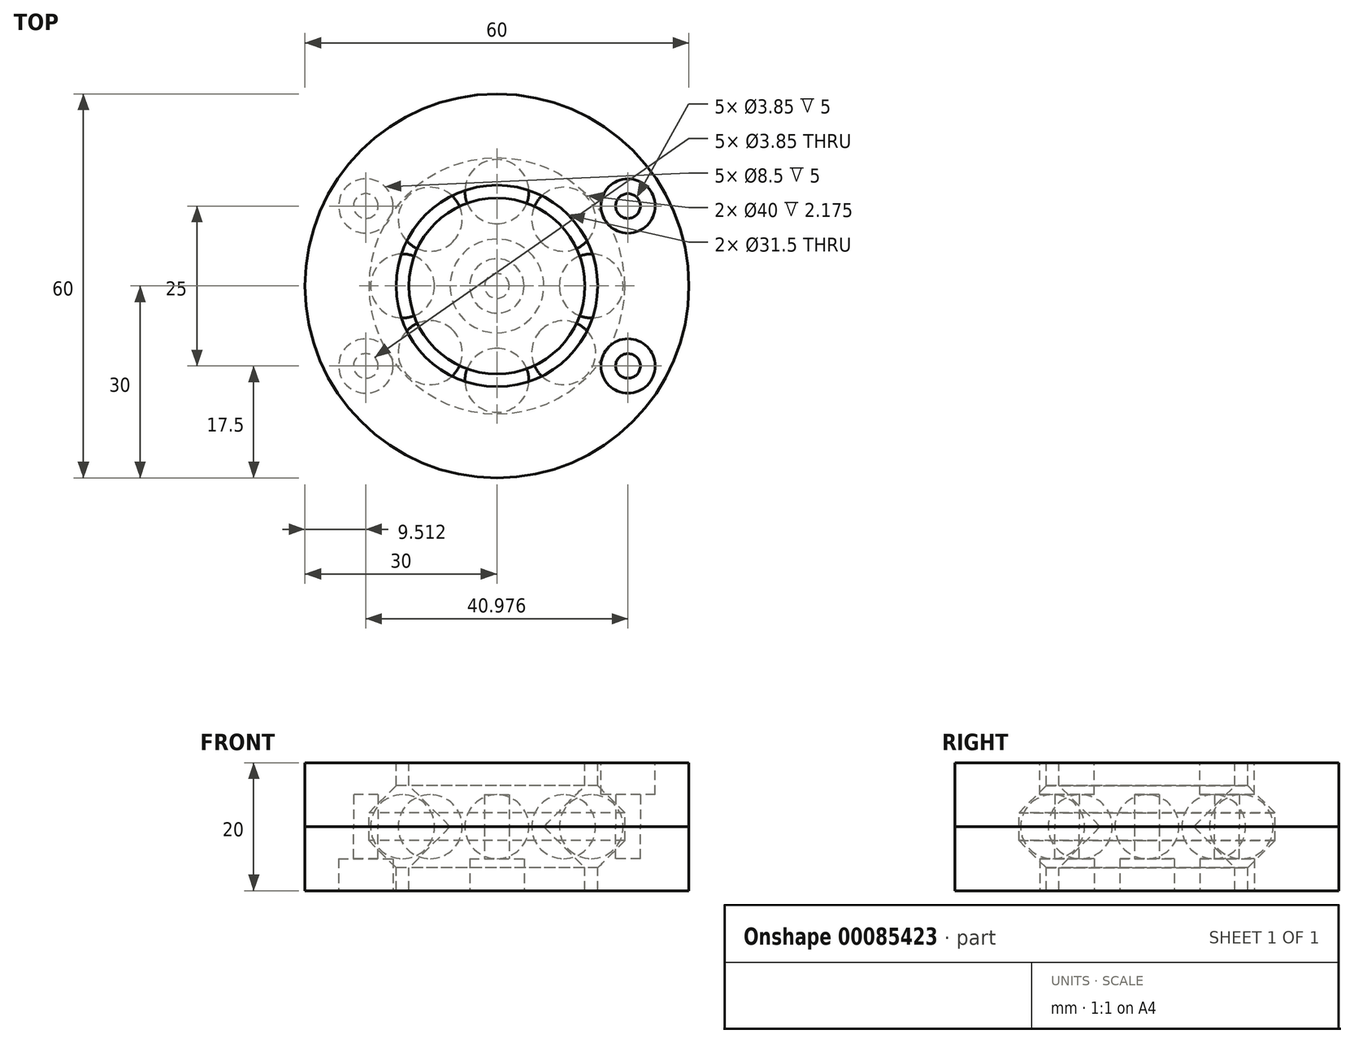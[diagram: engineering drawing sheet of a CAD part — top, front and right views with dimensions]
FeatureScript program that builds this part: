
annotation { "Feature Type Name" : "Feature", "Feature Type Description" : "" }
export const myFeature = defineFeature(function(context is Context, id is Id, definition is map)
    precondition{}
    {
        {
            var Q0;
            Q0=qCreatedBy(makeId("Front.planeOp"),FACE);
            var sketch = newSketch(context, id + "F0", { "sketchPlane" : qUnion([Q0])});
            skLineSegment(sketch, "E0.bottom", {"start": v(13.75, -10) * mm, "end": v(-13.75, -10) * mm, "construction": true});
            skLineSegment(sketch, "E0.top", {"start": v(13.75, 10) * mm, "end": v(-13.75, 10) * mm, "construction": true});
            skLineSegment(sketch, "E0.left", {"start": v(13.75, -10) * mm, "end": v(13.75, 10) * mm, "construction": true});
            skLineSegment(sketch, "E0.right", {"start": v(-13.75, -10) * mm, "end": v(-13.75, 10) * mm, "construction": true});
            skPoint(sketch, "E0.middle", {"position": v(0, 0) * mm});
            skLineSegment(sketch, "E1.bottom", {"start": v(30, -10) * mm, "end": v(-30, -10) * mm, "construction": true});
            skLineSegment(sketch, "E1.top", {"start": v(30, 10) * mm, "end": v(-30, 10) * mm, "construction": true});
            skLineSegment(sketch, "E1.left", {"start": v(30, -10) * mm, "end": v(30, 10) * mm, "construction": true});
            skLineSegment(sketch, "E1.right", {"start": v(-30, -10) * mm, "end": v(-30, 10) * mm, "construction": true});
            skLineSegment(sketch, "E2.bottom", {"start": v(-13.75, 10) * mm, "end": v(-15.75, 10) * mm, "construction": true});
            skLineSegment(sketch, "E2.top", {"start": v(-13.75, -10) * mm, "end": v(-15.75, -10) * mm, "construction": true});
            skLineSegment(sketch, "E2.left", {"start": v(-13.75, 10) * mm, "end": v(-13.75, -10) * mm, "construction": true});
            skLineSegment(sketch, "E2.right", {"start": v(-15.75, 10) * mm, "end": v(-15.75, -10) * mm, "construction": true});
            skLineSegment(sketch, "E3.bottom", {"start": v(13.75, 10) * mm, "end": v(15.75, 10) * mm, "construction": true});
            skLineSegment(sketch, "E3.top", {"start": v(13.75, -10) * mm, "end": v(15.75, -10) * mm, "construction": true});
            skLineSegment(sketch, "E3.left", {"start": v(13.75, 10) * mm, "end": v(13.75, -10) * mm, "construction": true});
            skLineSegment(sketch, "E3.right", {"start": v(15.75, 10) * mm, "end": v(15.75, -10) * mm, "construction": true});
            skLineSegment(sketch, "E4", {"start": v(-14.75, 10) * mm, "end": v(-14.75, -10) * mm, "construction": true});
            skLineSegment(sketch, "E5", {"start": v(14.75, 10) * mm, "end": v(14.75, -10) * mm, "construction": true});
            skLineSegment(sketch, "E6", {"start": v(-30, 0) * mm, "end": v(30, 0) * mm, "construction": true});
            skCircle(sketch, "E7", {"center": v(-14.75, 0) * mm, "radius": 5 * mm, "construction": true});
            skCircle(sketch, "E8", {"center": v(14.75, 0) * mm, "radius": 5 * mm, "construction": true});
            skLineSegment(sketch, "E9", {"start": v(-15.75, -6.42) * mm, "end": v(-22.17, 0) * mm, "construction": true});
            skLineSegment(sketch, "E10", {"start": v(-22.17, 0) * mm, "end": v(-15.75, 6.42) * mm, "construction": true});
            skLineSegment(sketch, "E11", {"start": v(-30, 0) * mm, "end": v(-30, -10) * mm});
            skLineSegment(sketch, "E12", {"start": v(-30, -10) * mm, "end": v(-15.75, -10) * mm});
            skLineSegment(sketch, "E13", {"start": v(-15.75, -10) * mm, "end": v(-15.75, -6.42) * mm});
            skLineSegment(sketch, "E14", {"start": v(-15.75, -6.42) * mm, "end": v(-13.75, -6.42) * mm, "construction": true});
            skLineSegment(sketch, "E15", {"start": v(-13.75, -6.42) * mm, "end": v(-7.33, 0) * mm, "construction": true});
            skLineSegment(sketch, "E16", {"start": v(-7.33, 0) * mm, "end": v(-13.75, 6.42) * mm, "construction": true});
            skLineSegment(sketch, "E17", {"start": v(-13.75, 6.42) * mm, "end": v(-15.75, 6.42) * mm, "construction": true});
            skLineSegment(sketch, "E18", {"start": v(0, 10) * mm, "end": v(0, -10) * mm, "construction": true});
            skLineSegment(sketch, "E19", {"start": v(-13.75, -10) * mm, "end": v(-13.75, -6.42) * mm});
            skLineSegment(sketch, "E20", {"start": v(-13.75, -6.42) * mm, "end": v(-7.33, 0) * mm});
            skLineSegment(sketch, "E21", {"start": v(-7.33, 0) * mm, "end": v(0, 0) * mm});
            skLineSegment(sketch, "E22", {"start": v(0, 0) * mm, "end": v(0, -10) * mm});
            skLineSegment(sketch, "E23", {"start": v(0, -10) * mm, "end": v(-13.75, -10) * mm});
            skPoint(sketch, "E24", {"position": v(-14.75, 5) * mm});
            skPoint(sketch, "E25", {"position": v(-14.75, -5) * mm});
            skArc(sketch, "E26", {"start": v(-14.75, 5) * mm, "mid": v(-19.75, 0) * mm, "end": v(-14.75, -5) * mm});
            skLineSegment(sketch, "E27", {"start": v(-14.75, 5) * mm, "end": v(-14.75, -5) * mm});
            skLineSegment(sketch, "E28", {"start": v(-15.75, 6.42) * mm, "end": v(-15.75, 10) * mm});
            skLineSegment(sketch, "E29", {"start": v(-15.75, 10) * mm, "end": v(-30, 10) * mm});
            skLineSegment(sketch, "E30", {"start": v(-30, 10) * mm, "end": v(-30, 0) * mm});
            skLineSegment(sketch, "E31", {"start": v(-7.33, 0) * mm, "end": v(-13.75, 6.42) * mm});
            skLineSegment(sketch, "E32", {"start": v(-13.75, 6.42) * mm, "end": v(-13.75, 10) * mm});
            skLineSegment(sketch, "E33", {"start": v(-13.75, 10) * mm, "end": v(0, 10) * mm});
            skLineSegment(sketch, "E34", {"start": v(0, 10) * mm, "end": v(0, 0) * mm});
            skLineSegment(sketch, "E35", {"start": v(-20, 2.17) * mm, "end": v(-20, -2.17) * mm, "construction": true});
            skLineSegment(sketch, "E36", {"start": v(-15.75, 6.42) * mm, "end": v(-20, 2.17) * mm});
            skLineSegment(sketch, "E37", {"start": v(-20, 2.17) * mm, "end": v(-20, 0) * mm});
            skLineSegment(sketch, "E38", {"start": v(-20, 0) * mm, "end": v(-30, 0) * mm});
            skLineSegment(sketch, "E39", {"start": v(-20, 0) * mm, "end": v(-20, -2.17) * mm});
            skLineSegment(sketch, "E40", {"start": v(-20, -2.17) * mm, "end": v(-15.75, -6.42) * mm});
            skSolve(sketch);
        }
        {
            var Q0;
            Q0=makeQuery(id+"F0.imprint","IMPRINT",FACE,{"disambiguationData":[TD([[makeQuery(id+"F0.imprint","IMPRINT",EDGE,{"derivedFrom":sQuery(id+"F0.wireOp",EDGE,"E11")}),1.0]])]});
            var Q1;
            Q1=sQuery(id+"F0.wireOp",EDGE,"E22");
            revolve(context, id + "F1", {"entities" : qUnion([Q0]), "axis" : qUnion([Q1]), "revolveType" : RevolveType.FULL});
        }
        {
            var Q0;
            Q0=makeQuery(id+"F0.imprint","IMPRINT",FACE,{"disambiguationData":[TD([[makeQuery(id+"F0.imprint","IMPRINT",EDGE,{"derivedFrom":sQuery(id+"F0.wireOp",EDGE,"LGbsAvZm-hPPb-qug5-25sG-ZA0GaCGVv74Y")}),-1.0]])]});
            var Q1;
            Q1=makeQuery(id+"F0.imprint","IMPRINT",FACE,{"disambiguationData":[TD([[makeQuery(id+"F0.imprint","IMPRINT",EDGE,{"derivedFrom":sQuery(id+"F0.wireOp",EDGE,"E28")}),1.0]])]});
            var Q2;
            Q2=sQuery(id+"F0.wireOp",EDGE,"E18");
            revolve(context, id + "F2", {"entities" : qUnion([Q0, Q1]), "axis" : qUnion([Q2]), "revolveType" : RevolveType.FULL});
        }
        {
            var Q0;
            Q0=makeQuery(id+"F0.imprint","IMPRINT",FACE,{"disambiguationData":[TD([[makeQuery(id+"F0.imprint","IMPRINT",EDGE,{"derivedFrom":sQuery(id+"F0.wireOp",EDGE,"E19")}),-1.0]])]});
            var Q1;
            Q1=sQuery(id+"F0.wireOp",EDGE,"E22");
            revolve(context, id + "F3", {"entities" : qUnion([Q0]), "axis" : qUnion([Q1]), "revolveType" : RevolveType.FULL});
        }
        {
            var Q0;
            Q0=makeQuery(id+"F0.imprint","IMPRINT",FACE,{"disambiguationData":[TD([[makeQuery(id+"F0.imprint","IMPRINT",EDGE,{"derivedFrom":sQuery(id+"F0.wireOp",EDGE,"E21")}),1.0]])]});
            var Q1;
            Q1=sQuery(id+"F0.wireOp",EDGE,"E34");
            revolve(context, id + "F4", {"entities" : qUnion([Q0]), "axis" : qUnion([Q1]), "revolveType" : RevolveType.FULL});
        }
        {
            var Q0;
            Q0=makeQuery(id+"F0.imprint","IMPRINT",FACE,{"disambiguationData":[TD([[makeQuery(id+"F0.imprint","IMPRINT",EDGE,{"derivedFrom":sQuery(id+"F0.wireOp",EDGE,"E26")}),1.0]])]});
            var Q1;
            Q1=sQuery(id+"F0.wireOp",EDGE,"E27");
            revolve(context, id + "F5", {"entities" : qUnion([Q0]), "axis" : qUnion([Q1]), "revolveType" : RevolveType.FULL});
        }
        {
            var Q0;
            Q0=makeQuery(id+"F5.opRevolve","SWEPT_BODY",BODY,{"disambiguationData":[OSD([sQuery(id+"F0.wireOp",EDGE,"E26"),sQuery(id+"F0.wireOp",EDGE,"E27")])]});
            var Q1;
            Q1=sQuery(id+"F0.wireOp",EDGE,"E34");
            circularPattern(context, id + "F6", {"entities" : qUnion([Q0]), "axis" : qUnion([Q1]), "angle" : 45 * degree, "instanceCount" : 8});
        }
        {
            var Q0;
            Q0=makeQuery(id+"F3.opRevolve","SWEPT_FACE",FACE,{"disambiguationData":[OSD([sQuery(id+"F0.wireOp",EDGE,"E23")])]});
            var sketch = newSketch(context, id + "F7", { "sketchPlane" : qUnion([Q0])});
            skCircle(sketch, "E41", {"center": v(0, 0) * mm, "radius": 4.25 * mm});
            skCircle(sketch, "E42", {"center": v(0, 0) * mm, "radius": 1.93 * mm});
            skSolve(sketch);
        }
        {
            var Q0;
            Q0 = qSketchRegion(id + "F7", true);
            var Q1;
            Q1=makeQuery(id+"F7.imprint","IMPRINT",FACE,{"disambiguationData":[TD([[makeQuery(id+"F7.imprint","IMPRINT",EDGE,{"derivedFrom":sQuery(id+"F7.wireOp",EDGE,"E42")}),1.0]])]});
            extrude(context, id + "F8", {"entities" : qUnion([Q0, Q1]), "operationType" : NewBodyOperationType.REMOVE, "oppositeDirection" : true, "depth" : 5 * mm});
        }
        {
            var Q0;
            Q0=makeQuery(id+"F7.imprint","IMPRINT",FACE,{"disambiguationData":[TD([[makeQuery(id+"F7.imprint","IMPRINT",EDGE,{"derivedFrom":sQuery(id+"F7.wireOp",EDGE,"E42")}),1.0]])]});
            extrude(context, id + "F9", {"entities" : qUnion([Q0]), "operationType" : NewBodyOperationType.REMOVE, "oppositeDirection" : true, "depth" : 15 * mm});
        }
        {
            var Q0;
            Q0=qCreatedBy(makeId("Top.planeOp"),FACE);
            var sketch = newSketch(context, id + "F10", { "sketchPlane" : qUnion([Q0])});
            skCircle(sketch, "E43", {"center": v(0, 0) * mm, "radius": 20 * mm, "construction": true});
            skLineSegment(sketch, "E44", {"start": v(0, 0) * mm, "end": v(20, 0) * mm, "construction": true});
            skPoint(sketch, "E45", {"position": v(24, 0) * mm});
            skCircle(sketch, "E46", {"center": v(0, 0) * mm, "radius": 24 * mm, "construction": true});
            skCircle(sketch, "E47", {"center": v(20.49, -12.5) * mm, "radius": 1.93 * mm, "construction": true});
            skLineSegment(sketch, "E48", {"start": v(20.49, -12.5) * mm, "end": v(20.49, 12.5) * mm, "construction": true});
            skCircle(sketch, "E49", {"center": v(20.49, 12.5) * mm, "radius": 1.93 * mm, "construction": true});
            skCircle(sketch, "E50", {"center": v(20.49, 12.5) * mm, "radius": 1.93 * mm});
            skCircle(sketch, "E51", {"center": v(20.49, -12.5) * mm, "radius": 1.93 * mm});
            skLineSegment(sketch, "E52", {"start": v(20.49, -12.5) * mm, "end": v(-20.49, -12.5) * mm, "construction": true});
            skLineSegment(sketch, "E53", {"start": v(20.49, 12.5) * mm, "end": v(-20.49, 12.5) * mm, "construction": true});
            skLineSegment(sketch, "E54", {"start": v(-20.49, 12.5) * mm, "end": v(-20.49, -12.5) * mm, "construction": true});
            skCircle(sketch, "E55", {"center": v(-20.49, -12.5) * mm, "radius": 1.93 * mm});
            skCircle(sketch, "E56", {"center": v(-20.49, 12.5) * mm, "radius": 1.93 * mm});
            skCircle(sketch, "E57", {"center": v(0, 0) * mm, "radius": 30 * mm, "construction": true});
            skLineSegment(sketch, "E58", {"start": v(20, 0) * mm, "end": v(24, 0) * mm, "construction": true});
            skLineSegment(sketch, "E59", {"start": v(24, 0) * mm, "end": v(30, 0) * mm, "construction": true});
            skSolve(sketch);
        }
        {
            var Q0;
            Q0 = qSketchRegion(id + "F10", true);
            extrude(context, id + "F11", {"entities" : qUnion([Q0]), "operationType" : NewBodyOperationType.REMOVE, "oppositeDirection" : true, "depth" : 5 * mm});
        }
        {
            var Q0;
            Q0=makeQuery(id+"F10.imprint","IMPRINT",FACE,{"disambiguationData":[TD([[makeQuery(id+"F10.imprint","IMPRINT",EDGE,{"derivedFrom":sQuery(id+"F10.wireOp",EDGE,"E51")}),1.0]])]});
            var Q1;
            Q1=makeQuery(id+"F10.imprint","IMPRINT",FACE,{"disambiguationData":[TD([[makeQuery(id+"F10.imprint","IMPRINT",EDGE,{"derivedFrom":sQuery(id+"F10.wireOp",EDGE,"E50")}),1.0]])]});
            var Q2;
            Q2=makeQuery(id+"F10.imprint","IMPRINT",FACE,{"disambiguationData":[TD([[makeQuery(id+"F10.imprint","IMPRINT",EDGE,{"derivedFrom":sQuery(id+"F10.wireOp",EDGE,"E55")}),1.0]])]});
            var Q3;
            Q3=makeQuery(id+"F10.imprint","IMPRINT",FACE,{"disambiguationData":[TD([[makeQuery(id+"F10.imprint","IMPRINT",EDGE,{"derivedFrom":sQuery(id+"F10.wireOp",EDGE,"E56")}),1.0]])]});
            extrude(context, id + "F12", {"entities" : qUnion([Q0, Q1, Q2, Q3]), "operationType" : NewBodyOperationType.REMOVE, "depth" : 5 * mm});
        }
        {
            var Q0;
            Q0=makeQuery(id+"F2.opRevolve","SWEPT_FACE",FACE,{"disambiguationData":[OSD([sQuery(id+"F0.wireOp",EDGE,"E29")])]});
            var sketch = newSketch(context, id + "F13", { "sketchPlane" : qUnion([Q0])});
            skCircle(sketch, "E60", {"center": v(20.49, 12.5) * mm, "radius": 4.25 * mm});
            skCircle(sketch, "E61", {"center": v(20.49, -12.5) * mm, "radius": 4.25 * mm});
            skSolve(sketch);
        }
        {
            var Q0;
            Q0=makeQuery(id+"F13.imprint","IMPRINT",FACE,{"disambiguationData":[TD([[makeQuery(id+"F13.imprint","IMPRINT",EDGE,{"derivedFrom":sQuery(id+"F13.wireOp",EDGE,"E61")}),1.0]])]});
            var Q1;
            Q1=makeQuery(id+"F13.imprint","IMPRINT",FACE,{"disambiguationData":[TD([[makeQuery(id+"F13.imprint","IMPRINT",EDGE,{"derivedFrom":sQuery(id+"F13.wireOp",EDGE,"E60")}),1.0]])]});
            extrude(context, id + "F14", {"entities" : qUnion([Q0, Q1]), "operationType" : NewBodyOperationType.REMOVE, "oppositeDirection" : true, "depth" : 5 * mm});
        }
        {
            var Q0;
            Q0=makeQuery(id+"F1.opRevolve","SWEPT_FACE",FACE,{"disambiguationData":[OSD([sQuery(id+"F0.wireOp",EDGE,"E12")])]});
            var sketch = newSketch(context, id + "F15", { "sketchPlane" : qUnion([Q0])});
            skCircle(sketch, "E62", {"center": v(-20.49, 12.5) * mm, "radius": 4.25 * mm});
            skCircle(sketch, "E63", {"center": v(-20.49, -12.5) * mm, "radius": 4.25 * mm});
            skSolve(sketch);
        }
        {
            var Q0;
            Q0=makeQuery(id+"F15.imprint","IMPRINT",FACE,{"disambiguationData":[TD([[makeQuery(id+"F15.imprint","IMPRINT",EDGE,{"derivedFrom":sQuery(id+"F15.wireOp",EDGE,"E62")}),1.0]])]});
            var Q1;
            Q1=makeQuery(id+"F15.imprint","IMPRINT",FACE,{"disambiguationData":[TD([[makeQuery(id+"F15.imprint","IMPRINT",EDGE,{"derivedFrom":sQuery(id+"F15.wireOp",EDGE,"E63")}),1.0]])]});
            extrude(context, id + "F16", {"entities" : qUnion([Q0, Q1]), "operationType" : NewBodyOperationType.REMOVE, "oppositeDirection" : true, "depth" : 5 * mm});
        }
    });
